# Revit family: Arper_Aava-02_trestle-fixed_polypropylene_upholstery_7622
name_source: partatom
category: Furniture
units: mm (PartAtom-declared; Revit-internal decimal feet)

## family parameters
Always vertical = Yes
Cut with Voids When Loaded = No
OmniClass Number = 23.40.20.00
OmniClass Title = General Furniture and Specialties
Room Calculation Point = No
Shared = No
Work Plane-Based = No

## types (1)
- Arper_Aava-02_trestle-fixed_polypropylene_upholstery_7622
    Default Elevation = 0 mm  [stored 0 ft]
    Description = Chair on fixed trestle base in powder-coated aluminium, mounted on 
self-braking castors (of the same colour as the base). Shell in 
polypropylene made with post-consumer recycled materials, mixed 
with virgin material, with upholstery in fabric, leather, coated fabric or 
customer’s own material. The upholstery can be separated and 
replaced by technical personnel, since it has been applied without 
the use of glue. Optional armrests in the same colour as the base
are also available, equipped with pads in polypropylene or in the 
upholstered version.
    Manufacturer = ARPER s.p.a.
    Model = Aava 02
    URL = http://www.arper.com

note: [stored X ft] marks values corroborated as IEEE doubles in the binary element streams (Revit-internal decimal feet)
